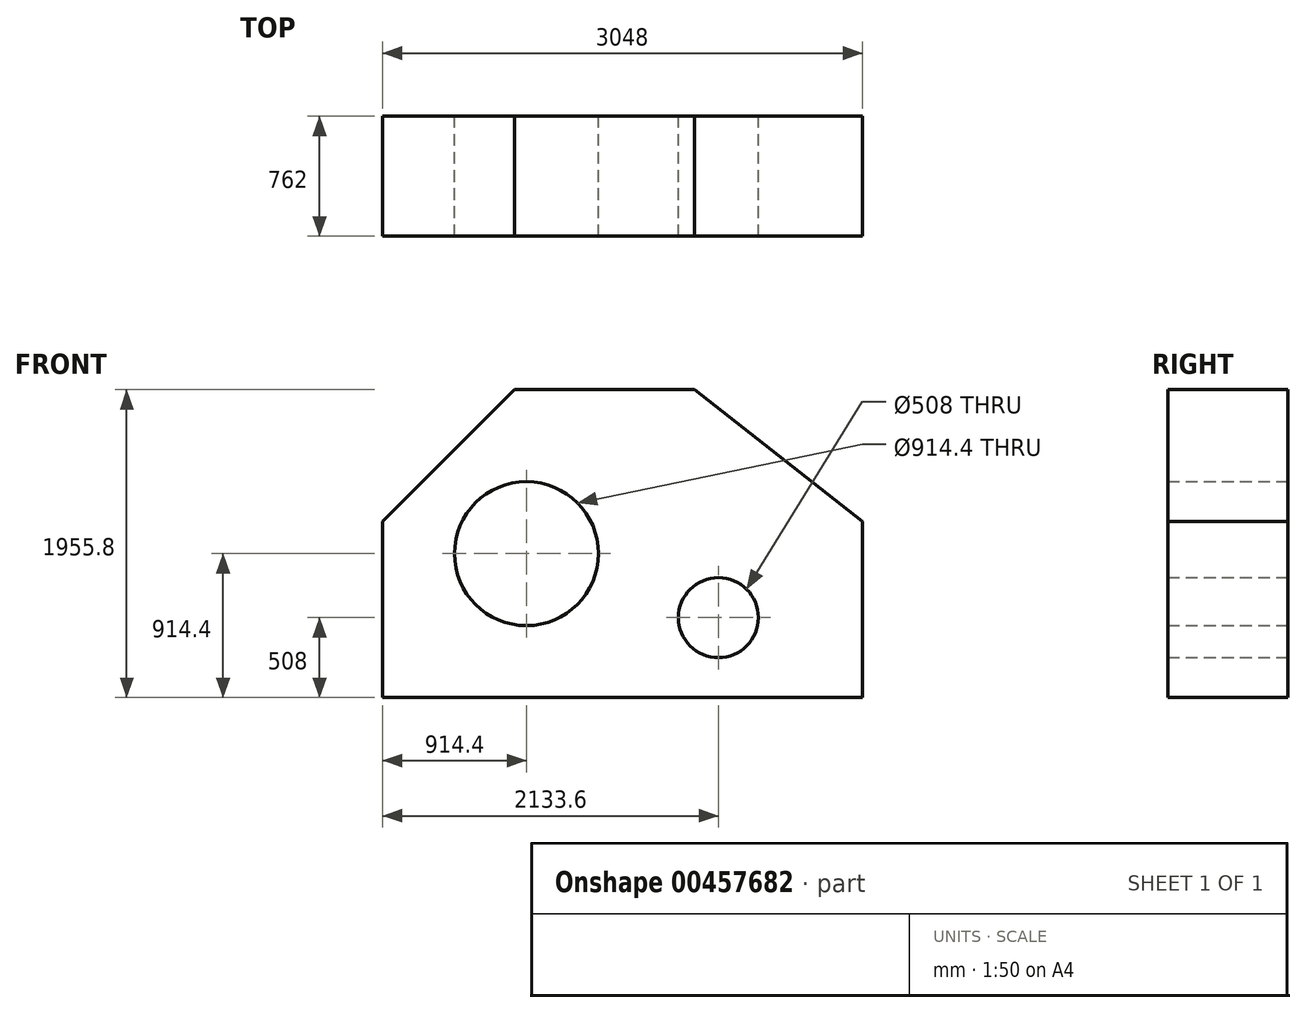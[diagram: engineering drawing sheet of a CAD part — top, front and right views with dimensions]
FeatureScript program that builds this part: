
annotation { "Feature Type Name" : "Feature", "Feature Type Description" : "" }
export const myFeature = defineFeature(function(context is Context, id is Id, definition is map)
    precondition{}
    {
        {
            var Q0;
            Q0=qCreatedBy(makeId("Front.planeOp"),FACE);
            var sketch = newSketch(context, id + "F0", { "sketchPlane" : qUnion([Q0])});
            skLineSegment(sketch, "E0", {"start": v(0, 0) * mm, "end": v(3048, 0) * mm});
            skLineSegment(sketch, "E1", {"start": v(0, 0) * mm, "end": v(0, 1117.6) * mm});
            skLineSegment(sketch, "E2", {"start": v(0, 1117.6) * mm, "end": v(838.2, 1955.8) * mm});
            skLineSegment(sketch, "E3", {"start": v(838.2, 1955.8) * mm, "end": v(1981.2, 1955.8) * mm});
            skCircle(sketch, "E4", {"center": v(2133.6, 508) * mm, "radius": 254 * mm});
            skCircle(sketch, "E5", {"center": v(914.4, 914.4) * mm, "radius": 457.2 * mm});
            skLineSegment(sketch, "E6", {"start": v(3048, 0) * mm, "end": v(3048, 1117.6) * mm});
            skLineSegment(sketch, "E7", {"start": v(3048, 1117.6) * mm, "end": v(1981.2, 1955.8) * mm});
            skSolve(sketch);
        }
        {
            var Q0;
            Q0=makeQuery(id+"F0.imprint","IMPRINT",FACE,{"disambiguationData":[TD([[makeQuery(id+"F0.imprint","IMPRINT",EDGE,{"derivedFrom":sQuery(id+"F0.wireOp",EDGE,"E0")}),1.0]])]});
            extrude(context, id + "F1", {"entities" : qUnion([Q0]), "depth" : 762 * mm});
        }
    });
